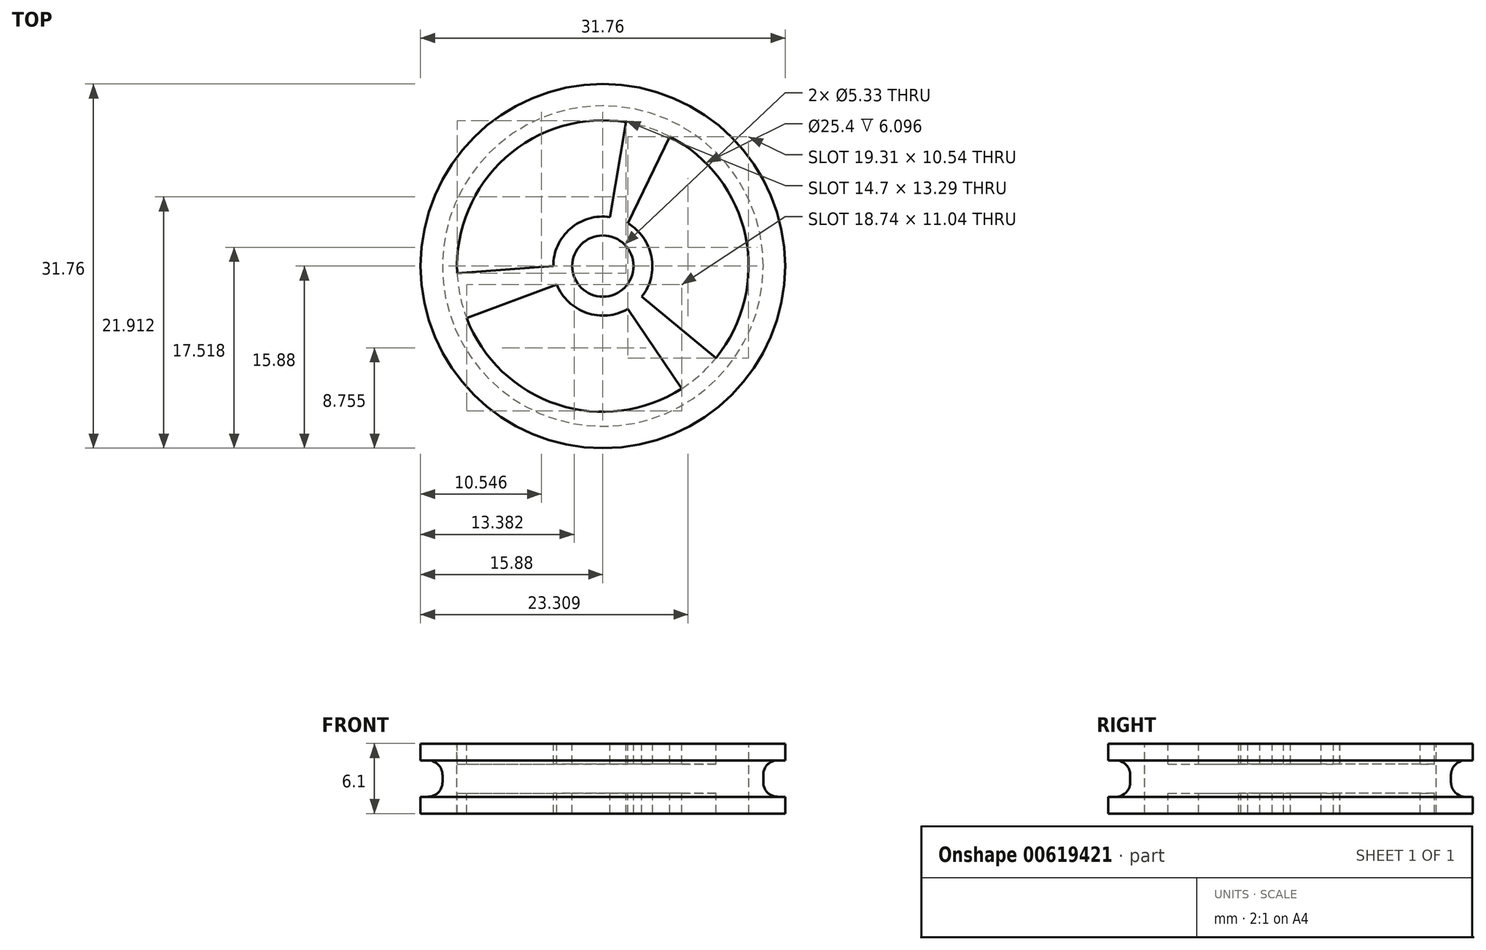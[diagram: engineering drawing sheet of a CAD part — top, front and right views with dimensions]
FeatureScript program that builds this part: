
annotation { "Feature Type Name" : "Feature", "Feature Type Description" : "" }
export const myFeature = defineFeature(function(context is Context, id is Id, definition is map)
    precondition{}
    {
        {
            var Q0;
            Q0=qCreatedBy(makeId("Top.planeOp"),FACE);
            var sketch = newSketch(context, id + "F0", { "sketchPlane" : qUnion([Q0])});
            skCircle(sketch, "E0", {"center": v(0, 0) * mm, "radius": 15.88 * mm});
            skSolve(sketch);
        }
        {
            var Q0;
            Q0 = qSketchRegion(id + "F0", true);
            extrude(context, id + "F1", {"entities" : qUnion([Q0]), "endBound" : BoundingType.SYMMETRIC, "depth" : 6.1 * mm, "offsetDistance" : 25.4 * mm});
        }
        {
            var Q0;
            Q0=qCreatedBy(makeId("Top.planeOp"),FACE);
            var sketch = newSketch(context, id + "F2", { "sketchPlane" : qUnion([Q0])});
            skCircle(sketch, "E1", {"center": v(0, 0) * mm, "radius": 13.97 * mm});
            skCircle(sketch, "E2", {"center": v(0, 0) * mm, "radius": 18 * mm});
            skSolve(sketch);
        }
        {
            var Q0;
            Q0 = qSketchRegion(id + "F2", true);
            extrude(context, id + "F3", {"entities" : qUnion([Q0]), "operationType" : NewBodyOperationType.REMOVE, "endBound" : BoundingType.SYMMETRIC, "oppositeDirection" : true, "depth" : 3.17 * mm, "offsetDistance" : 25.4 * mm});
        }
        {
            var Q0;
            Q0=makeQuery(id+"F1.opExtrude","CAP_FACE",FACE,{"disambiguationData":[OSD([sQuery(id+"F0.wireOp",EDGE,"E0")])],"isStart":false});
            var sketch = newSketch(context, id + "F4", { "sketchPlane" : qUnion([Q0])});
            skArc(sketch, "E3", {"start": v(2.02, 12.54) * mm, "mid": v(-8.47, 9.47) * mm, "end": v(-12.69, -0.61) * mm});
            skPoint(sketch, "E4.orphan", {"position": v(-0.64, 0.64) * mm});
            skPoint(sketch, "E5.orphan", {"position": v(-0.23, -0.87) * mm});
            skPoint(sketch, "E6.orphan", {"position": v(0.87, 0.23) * mm});
            skArc(sketch, "E7.trimOffspring", {"start": v(0.61, 4.27) * mm, "mid": v(-2.83, 3.26) * mm, "end": v(-4.32, 0) * mm});
            skCircle(sketch, "E8", {"center": v(0, 0) * mm, "radius": 2.67 * mm});
            skLineSegment(sketch, "E9.trimOffspring", {"start": v(-4.32, 0) * mm, "end": v(-12.69, -0.61) * mm});
            skLineSegment(sketch, "E10.trimOffspring", {"start": v(0.61, 4.27) * mm, "end": v(2.02, 12.54) * mm});
            skArc(sketch, "E11.1.0", {"start": v(-4, -1.6) * mm, "mid": v(-1.41, -4.08) * mm, "end": v(2.16, -3.74) * mm});
            skLineSegment(sketch, "E11.1.1", {"start": v(-4, -1.6) * mm, "end": v(-11.87, -4.52) * mm});
            skArc(sketch, "E11.1.2", {"start": v(-11.87, -4.52) * mm, "mid": v(-3.96, -12.07) * mm, "end": v(6.87, -10.68) * mm});
            skLineSegment(sketch, "E11.1.3", {"start": v(2.16, -3.74) * mm, "end": v(6.87, -10.68) * mm});
            skArc(sketch, "E11.2.0", {"start": v(3.4, -2.67) * mm, "mid": v(4.24, 0.82) * mm, "end": v(2.16, 3.74) * mm});
            skLineSegment(sketch, "E11.2.1", {"start": v(3.4, -2.67) * mm, "end": v(9.85, -8.02) * mm});
            skArc(sketch, "E11.2.2", {"start": v(9.85, -8.02) * mm, "mid": v(12.43, 2.6) * mm, "end": v(5.81, 11.3) * mm});
            skLineSegment(sketch, "E11.2.3", {"start": v(2.16, 3.74) * mm, "end": v(5.81, 11.3) * mm});
            skSolve(sketch);
        }
        {
            var Q0;
            Q0 = qSketchRegion(id + "F4", true);
            extrude(context, id + "F5", {"entities" : qUnion([Q0]), "operationType" : NewBodyOperationType.REMOVE, "endBound" : BoundingType.THROUGH_ALL, "oppositeDirection" : true, "depth" : 25.4 * mm, "offsetDistance" : 25.4 * mm});
        }
        {
            var Q0;
            Q0=makeQuery(id+"F3.boolean.opBoolean","COPY",EDGE,{"derivedFrom":makeQuery(id+"F3.opExtrude","CAP_EDGE",EDGE,{"disambiguationData":[OSD([sQuery(id+"F2.wireOp",EDGE,"E1")])],"isStart":false})});
            var Q1;
            Q1=makeQuery(id+"F3.boolean.opBoolean","COPY",EDGE,{"derivedFrom":makeQuery(id+"F3.opExtrude","CAP_EDGE",EDGE,{"disambiguationData":[OSD([sQuery(id+"F2.wireOp",EDGE,"E1")])],"isStart":true})});
            fillet(context, id + "F6", {"entities" : qUnion([Q0, Q1]), "radius" : 1.27 * mm, "tangentPropagation" : true, "allowEdgeOverflow" : false});
        }
        {
            var Q0;
            Q0=qCreatedBy(makeId("Top.planeOp"),FACE);
            var sketch = newSketch(context, id + "F7", { "sketchPlane" : qUnion([Q0])});
            skCircle(sketch, "E12", {"center": v(0, 0) * mm, "radius": 12.7 * mm});
            skSolve(sketch);
        }
        {
            var Q0;
            Q0 = qSketchRegion(id + "F7", true);
            extrude(context, id + "F8", {"entities" : qUnion([Q0]), "operationType" : NewBodyOperationType.REMOVE, "endBound" : BoundingType.SYMMETRIC, "oppositeDirection" : true, "depth" : 2.54 * mm, "offsetDistance" : 25.4 * mm});
        }
    });
